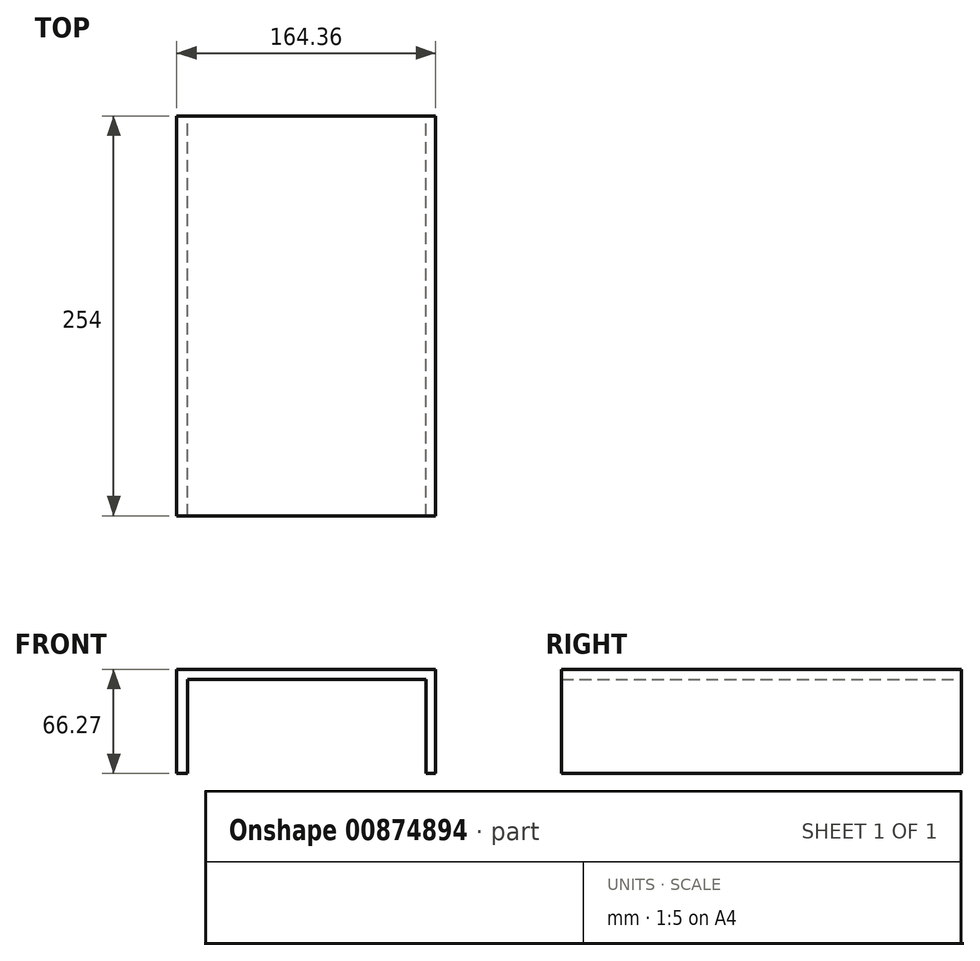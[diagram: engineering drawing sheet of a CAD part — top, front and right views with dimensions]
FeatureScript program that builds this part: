
annotation { "Feature Type Name" : "Feature", "Feature Type Description" : "" }
export const myFeature = defineFeature(function(context is Context, id is Id, definition is map)
    precondition{}
    {
        {
            var Q0;
            Q0=qCreatedBy(makeId("Front.planeOp"),FACE);
            var sketch = newSketch(context, id + "F0", { "sketchPlane" : qUnion([Q0])});
            skLineSegment(sketch, "E0", {"start": v(-64.67, -37.9) * mm, "end": v(-64.67, 28.07) * mm});
            skLineSegment(sketch, "E1", {"start": v(-64.67, 28.07) * mm, "end": v(99.69, 28.07) * mm});
            skLineSegment(sketch, "E2", {"start": v(99.69, 28.07) * mm, "end": v(99.69, -37.9) * mm});
            skLineSegment(sketch, "E3", {"start": v(-57.73, -38.2) * mm, "end": v(-57.73, 21.7) * mm});
            skLineSegment(sketch, "E4", {"start": v(-57.73, 21.7) * mm, "end": v(93.61, 21.7) * mm});
            skLineSegment(sketch, "E5", {"start": v(93.61, 21.7) * mm, "end": v(93.61, -37.9) * mm});
            skLineSegment(sketch, "E6", {"start": v(-57.73, -38.2) * mm, "end": v(-64.67, -37.9) * mm});
            skLineSegment(sketch, "E7", {"start": v(93.61, -37.9) * mm, "end": v(99.69, -37.9) * mm});
            skSolve(sketch);
        }
        {
            var Q0;
            Q0 = qSketchRegion(id + "F0", true);
            extrude(context, id + "F1", {"entities" : qUnion([Q0]), "depth" : 254 * mm, "offsetDistance" : 25.4 * mm});
        }
    });
